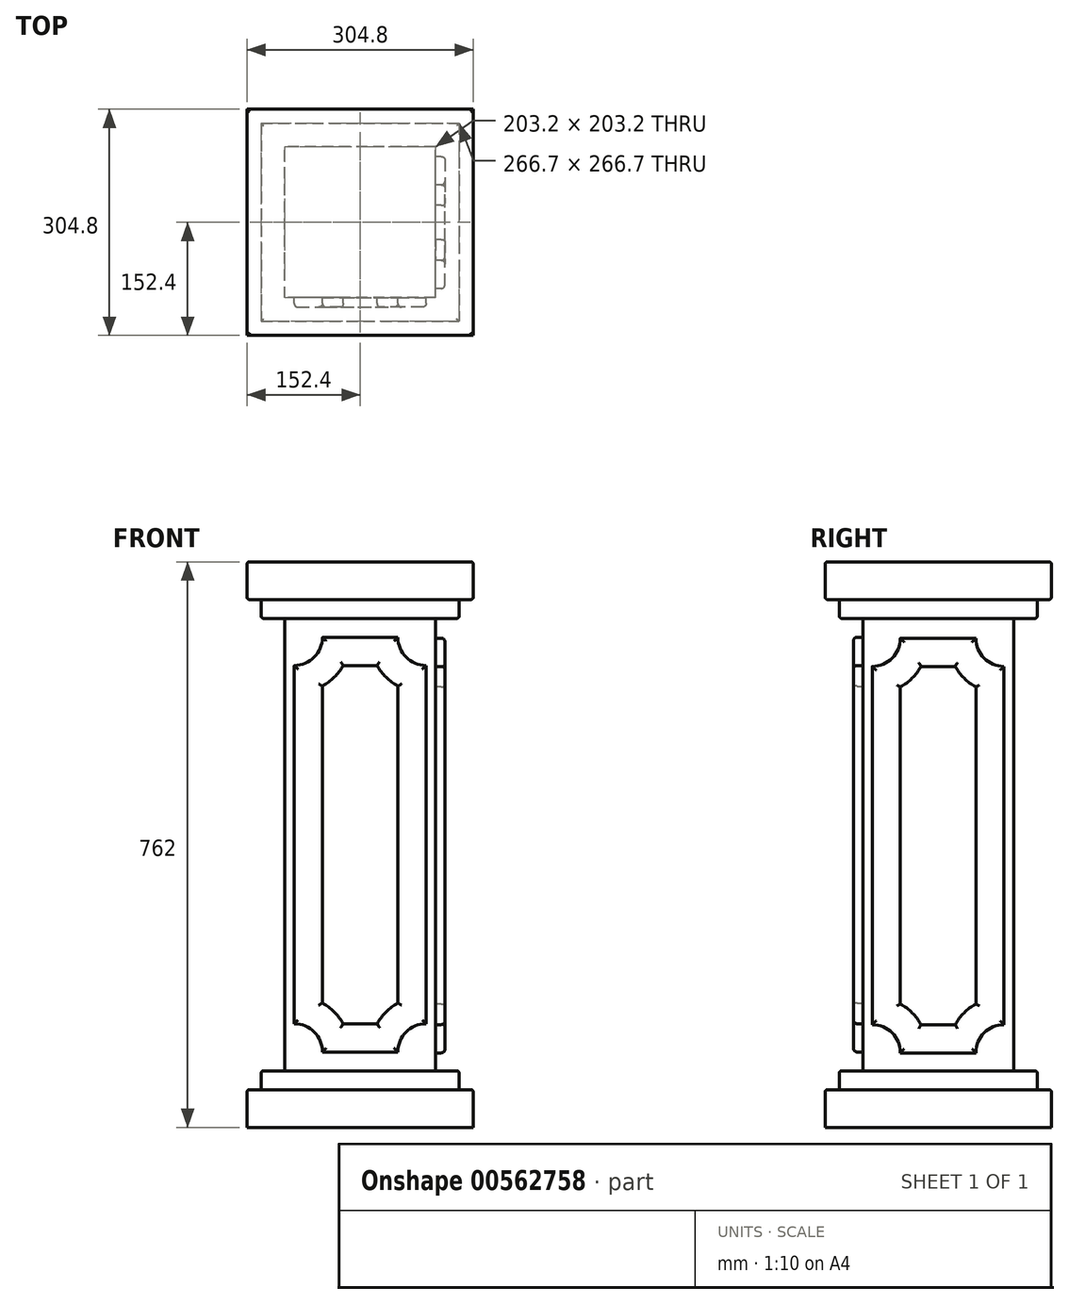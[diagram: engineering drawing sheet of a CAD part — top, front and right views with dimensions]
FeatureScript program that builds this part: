
annotation { "Feature Type Name" : "Feature", "Feature Type Description" : "" }
export const myFeature = defineFeature(function(context is Context, id is Id, definition is map)
    precondition{}
    {
        {
            var Q0;
            Q0=qCreatedBy(makeId("Top.planeOp"),FACE);
            var sketch = newSketch(context, id + "F0", { "sketchPlane" : qUnion([Q0])});
            skLineSegment(sketch, "E0.bottom", {"start": v(0, 0) * mm, "end": v(304.8, 0) * mm});
            skLineSegment(sketch, "E0.top", {"start": v(0, -304.8) * mm, "end": v(304.8, -304.8) * mm});
            skLineSegment(sketch, "E0.left", {"start": v(0, 0) * mm, "end": v(0, -304.8) * mm});
            skLineSegment(sketch, "E0.right", {"start": v(304.8, 0) * mm, "end": v(304.8, -304.8) * mm});
            skSolve(sketch);
        }
        {
            var Q0;
            Q0 = qSketchRegion(id + "F0", true);
            extrude(context, id + "F1", {"entities" : qUnion([Q0]), "depth" : 50.8 * mm, "offsetDistance" : 25.4 * mm});
        }
        {
            var Q0;
            Q0=makeQuery(id+"F1.opExtrude","CAP_FACE",FACE,{"disambiguationData":[OSD([sQuery(id+"F0.wireOp",EDGE,"E0.bottom"),sQuery(id+"F0.wireOp",EDGE,"E0.top"),sQuery(id+"F0.wireOp",EDGE,"E0.left"),sQuery(id+"F0.wireOp",EDGE,"E0.right")])],"isStart":false});
            var sketch = newSketch(context, id + "F2", { "sketchPlane" : qUnion([Q0])});
            skLineSegment(sketch, "E1.bottom", {"start": v(50.8, -50.8) * mm, "end": v(254, -50.8) * mm});
            skLineSegment(sketch, "E1.top", {"start": v(50.8, -254) * mm, "end": v(254, -254) * mm});
            skLineSegment(sketch, "E1.left", {"start": v(50.8, -50.8) * mm, "end": v(50.8, -254) * mm});
            skLineSegment(sketch, "E1.right", {"start": v(254, -50.8) * mm, "end": v(254, -254) * mm});
            skSolve(sketch);
        }
        {
            var Q0;
            Q0=makeQuery(id+"F2.imprint","IMPRINT",FACE,{"disambiguationData":[TD([[makeQuery(id+"F2.imprint","IMPRINT",EDGE,{"derivedFrom":sQuery(id+"F2.wireOp",EDGE,"E1.bottom")}),-1.0]])]});
            extrude(context, id + "F3", {"entities" : qUnion([Q0]), "operationType" : NewBodyOperationType.ADD, "depth" : 660.4 * mm, "offsetDistance" : 25.4 * mm});
        }
        {
            var Q0;
            Q0=makeQuery(id+"F3.opExtrude","CAP_FACE",FACE,{"disambiguationData":[OSD([sQuery(id+"F2.wireOp",EDGE,"E1.bottom"),sQuery(id+"F2.wireOp",EDGE,"E1.top"),sQuery(id+"F2.wireOp",EDGE,"E1.left"),sQuery(id+"F2.wireOp",EDGE,"E1.right")])],"isStart":false});
            var sketch = newSketch(context, id + "F4", { "sketchPlane" : qUnion([Q0])});
            skLineSegment(sketch, "E2.bottom", {"start": v(0, 0) * mm, "end": v(304.8, 0) * mm});
            skLineSegment(sketch, "E2.top", {"start": v(0, -304.8) * mm, "end": v(304.8, -304.8) * mm});
            skLineSegment(sketch, "E2.left", {"start": v(0, 0) * mm, "end": v(0, -304.8) * mm});
            skLineSegment(sketch, "E2.right", {"start": v(304.8, 0) * mm, "end": v(304.8, -304.8) * mm});
            skSolve(sketch);
        }
        {
            var Q0;
            Q0 = qSketchRegion(id + "F4", true);
            extrude(context, id + "F5", {"entities" : qUnion([Q0]), "operationType" : NewBodyOperationType.ADD, "depth" : 50.8 * mm, "offsetDistance" : 25.4 * mm});
        }
        {
            var Q0;
            Q0=makeQuery(id+"F1.opExtrude","CAP_FACE",FACE,{"disambiguationData":[OSD([sQuery(id+"F0.wireOp",EDGE,"E0.bottom"),sQuery(id+"F0.wireOp",EDGE,"E0.top"),sQuery(id+"F0.wireOp",EDGE,"E0.left"),sQuery(id+"F0.wireOp",EDGE,"E0.right")])],"isStart":false});
            var sketch = newSketch(context, id + "F6", { "sketchPlane" : qUnion([Q0])});
            skLineSegment(sketch, "E3.bottom", {"start": v(19.05, -19.05) * mm, "end": v(285.75, -19.05) * mm});
            skLineSegment(sketch, "E3.top", {"start": v(19.05, -285.75) * mm, "end": v(285.75, -285.75) * mm});
            skLineSegment(sketch, "E3.left", {"start": v(19.05, -19.05) * mm, "end": v(19.05, -285.75) * mm});
            skLineSegment(sketch, "E3.right", {"start": v(285.75, -19.05) * mm, "end": v(285.75, -285.75) * mm});
            skSolve(sketch);
        }
        {
            var Q0;
            Q0 = qSketchRegion(id + "F6", true);
            extrude(context, id + "F7", {"entities" : qUnion([Q0]), "operationType" : NewBodyOperationType.ADD, "depth" : 25.4 * mm, "offsetDistance" : 25.4 * mm});
        }
        {
            var Q0;
            Q0=makeQuery(id+"F5.opExtrude","CAP_FACE",FACE,{"disambiguationData":[OSD([sQuery(id+"F4.wireOp",EDGE,"E2.bottom"),sQuery(id+"F4.wireOp",EDGE,"E2.top"),sQuery(id+"F4.wireOp",EDGE,"E2.left"),sQuery(id+"F4.wireOp",EDGE,"E2.right")])],"isStart":true});
            var sketch = newSketch(context, id + "F8", { "sketchPlane" : qUnion([Q0])});
            skLineSegment(sketch, "E4.bottom", {"start": v(19.05, 285.75) * mm, "end": v(285.75, 285.75) * mm});
            skLineSegment(sketch, "E4.top", {"start": v(19.05, 19.05) * mm, "end": v(285.75, 19.05) * mm});
            skLineSegment(sketch, "E4.left", {"start": v(19.05, 285.75) * mm, "end": v(19.05, 19.05) * mm});
            skLineSegment(sketch, "E4.right", {"start": v(285.75, 285.75) * mm, "end": v(285.75, 19.05) * mm});
            skSolve(sketch);
        }
        {
            var Q0;
            Q0 = qSketchRegion(id + "F8", true);
            extrude(context, id + "F9", {"entities" : qUnion([Q0]), "operationType" : NewBodyOperationType.ADD, "depth" : 25.4 * mm, "offsetDistance" : 25.4 * mm});
        }
        {
            var Q0;
            Q0=makeQuery(id+"F7.opExtrude","CAP_EDGE",EDGE,{"disambiguationData":[OSD([sQuery(id+"F6.wireOp",EDGE,"E3.top")])],"isStart":false});
            var Q1;
            Q1=makeQuery(id+"F7.opExtrude","CAP_EDGE",EDGE,{"disambiguationData":[OSD([sQuery(id+"F6.wireOp",EDGE,"E3.right")])],"isStart":false});
            var Q2;
            Q2=makeQuery(id+"F7.opExtrude","CAP_EDGE",EDGE,{"disambiguationData":[OSD([sQuery(id+"F6.wireOp",EDGE,"E3.bottom")])],"isStart":false});
            var Q3;
            Q3=makeQuery(id+"F7.opExtrude","CAP_EDGE",EDGE,{"disambiguationData":[OSD([sQuery(id+"F6.wireOp",EDGE,"E3.left")])],"isStart":false});
            fillet(context, id + "F10", {"entities" : qUnion([Q0, Q1, Q2, Q3]), "radius" : 3.17 * mm, "tangentPropagation" : true, "allowEdgeOverflow" : false});
        }
        {
            var Q0;
            Q0=makeQuery(id+"F1.opExtrude","CAP_EDGE",EDGE,{"disambiguationData":[OSD([sQuery(id+"F0.wireOp",EDGE,"E0.right")])],"isStart":false});
            var Q1;
            Q1=makeQuery(id+"F1.opExtrude","CAP_EDGE",EDGE,{"disambiguationData":[OSD([sQuery(id+"F0.wireOp",EDGE,"E0.top")])],"isStart":false});
            var Q2;
            Q2=makeQuery(id+"F1.opExtrude","CAP_EDGE",EDGE,{"disambiguationData":[OSD([sQuery(id+"F0.wireOp",EDGE,"E0.left")])],"isStart":false});
            var Q3;
            Q3=makeQuery(id+"F1.opExtrude","CAP_EDGE",EDGE,{"disambiguationData":[OSD([sQuery(id+"F0.wireOp",EDGE,"E0.bottom")])],"isStart":false});
            fillet(context, id + "F11", {"entities" : qUnion([Q0, Q1, Q2, Q3]), "radius" : 3.17 * mm, "tangentPropagation" : true, "allowEdgeOverflow" : false});
        }
        {
            var Q0;
            Q0=makeQuery(id+"F9.opExtrude","CAP_EDGE",EDGE,{"disambiguationData":[OSD([sQuery(id+"F8.wireOp",EDGE,"E4.right")])],"isStart":false});
            var Q1;
            Q1=makeQuery(id+"F9.opExtrude","CAP_EDGE",EDGE,{"disambiguationData":[OSD([sQuery(id+"F8.wireOp",EDGE,"E4.bottom")])],"isStart":false});
            var Q2;
            Q2=makeQuery(id+"F9.opExtrude","CAP_EDGE",EDGE,{"disambiguationData":[OSD([sQuery(id+"F8.wireOp",EDGE,"E4.left")])],"isStart":false});
            var Q3;
            Q3=makeQuery(id+"F9.opExtrude","CAP_EDGE",EDGE,{"disambiguationData":[OSD([sQuery(id+"F8.wireOp",EDGE,"E4.top")])],"isStart":false});
            fillet(context, id + "F12", {"entities" : qUnion([Q0, Q1, Q2, Q3]), "radius" : 3.17 * mm, "tangentPropagation" : true, "allowEdgeOverflow" : false});
        }
        {
            var Q0;
            Q0=makeQuery(id+"F5.opExtrude","CAP_EDGE",EDGE,{"disambiguationData":[OSD([sQuery(id+"F4.wireOp",EDGE,"E2.top")])],"isStart":true});
            var Q1;
            Q1=makeQuery(id+"F5.opExtrude","CAP_EDGE",EDGE,{"disambiguationData":[OSD([sQuery(id+"F4.wireOp",EDGE,"E2.left")])],"isStart":true});
            var Q2;
            Q2=makeQuery(id+"F5.opExtrude","CAP_EDGE",EDGE,{"disambiguationData":[OSD([sQuery(id+"F4.wireOp",EDGE,"E2.bottom")])],"isStart":true});
            var Q3;
            Q3=makeQuery(id+"F5.opExtrude","CAP_EDGE",EDGE,{"disambiguationData":[OSD([sQuery(id+"F4.wireOp",EDGE,"E2.right")])],"isStart":true});
            fillet(context, id + "F13", {"entities" : qUnion([Q0, Q1, Q2, Q3]), "radius" : 3.17 * mm, "tangentPropagation" : true, "allowEdgeOverflow" : false});
        }
        {
            var Q0;
            Q0=makeQuery(id+"F3.opExtrude","SWEPT_FACE",FACE,{"disambiguationData":[OSD([sQuery(id+"F2.wireOp",EDGE,"E1.top")])]});
            var sketch = newSketch(context, id + "F14", { "sketchPlane" : qUnion([Q0])});
            skArc(sketch, "E5", {"start": v(63.5, 622.3) * mm, "mid": v(90.44, 633.46) * mm, "end": v(101.6, 660.4) * mm});
            skArc(sketch, "E6", {"start": v(203.2, 660.4) * mm, "mid": v(214.36, 633.46) * mm, "end": v(241.3, 622.3) * mm});
            skLineSegment(sketch, "E7", {"start": v(101.6, 660.4) * mm, "end": v(203.2, 660.4) * mm});
            skArc(sketch, "E8", {"start": v(63.5, 139.7) * mm, "mid": v(90.44, 128.54) * mm, "end": v(101.6, 101.6) * mm});
            skArc(sketch, "E9", {"start": v(203.2, 101.6) * mm, "mid": v(214.36, 128.54) * mm, "end": v(241.3, 139.7) * mm});
            skLineSegment(sketch, "E10", {"start": v(101.6, 101.6) * mm, "end": v(203.2, 101.6) * mm});
            skLineSegment(sketch, "E11", {"start": v(63.5, 139.7) * mm, "end": v(63.5, 622.3) * mm});
            skLineSegment(sketch, "E12", {"start": v(241.3, 622.3) * mm, "end": v(241.3, 139.7) * mm});
            skLineSegment(sketch, "E13", {"start": v(50.8, 373.92) * mm, "end": v(50.8, 596.34) * mm, "construction": true});
            skLineSegment(sketch, "E14", {"start": v(254, 370.37) * mm, "end": v(254, 598.7) * mm, "construction": true});
            skLineSegment(sketch, "E15", {"start": v(50.8, 76.2) * mm, "end": v(254, 76.2) * mm, "construction": true});
            skLineSegment(sketch, "E16", {"start": v(50.8, 685.8) * mm, "end": v(254, 685.8) * mm, "construction": true});
            skLineSegment(sketch, "E17.0", {"start": v(101.6, 167.6) * mm, "end": v(101.6, 594.4) * mm});
            skArc(sketch, "E17.1", {"start": v(101.6, 167.6) * mm, "mid": v(117.38, 155.48) * mm, "end": v(129.5, 139.7) * mm});
            skArc(sketch, "E17.2", {"start": v(101.6, 594.4) * mm, "mid": v(117.38, 606.52) * mm, "end": v(129.5, 622.3) * mm});
            skLineSegment(sketch, "E17.3", {"start": v(129.5, 139.7) * mm, "end": v(175.3, 139.7) * mm});
            skLineSegment(sketch, "E17.4", {"start": v(129.5, 622.3) * mm, "end": v(175.3, 622.3) * mm});
            skArc(sketch, "E17.5", {"start": v(175.3, 622.3) * mm, "mid": v(187.42, 606.52) * mm, "end": v(203.2, 594.4) * mm});
            skLineSegment(sketch, "E17.6", {"start": v(203.2, 594.4) * mm, "end": v(203.2, 167.6) * mm});
            skArc(sketch, "E17.7", {"start": v(175.3, 139.7) * mm, "mid": v(187.42, 155.48) * mm, "end": v(203.2, 167.6) * mm});
            skSolve(sketch);
        }
        {
            var Q0;
            Q0 = qSketchRegion(id + "F14", true);
            extrude(context, id + "F15", {"entities" : qUnion([Q0]), "operationType" : NewBodyOperationType.ADD, "depth" : 12.7 * mm, "offsetDistance" : 25.4 * mm});
        }
        {
            var Q0;
            Q0=makeQuery(id+"F3.opExtrude","SWEPT_FACE",FACE,{"disambiguationData":[OSD([sQuery(id+"F2.wireOp",EDGE,"E1.right")])]});
            var sketch = newSketch(context, id + "F16", { "sketchPlane" : qUnion([Q0])});
            skLineSegment(sketch, "E18", {"start": v(-101.6, -338.04) * mm, "end": v(101.6, -338.04) * mm, "construction": true});
            skLineSegment(sketch, "E19", {"start": v(-101.6, 685.8) * mm, "end": v(101.6, 685.8) * mm, "construction": true});
            skArc(sketch, "E20", {"start": v(-241.47, 621.09) * mm, "mid": v(-214.53, 632.25) * mm, "end": v(-203.37, 659.19) * mm});
            skArc(sketch, "E21", {"start": v(-101.77, 659.19) * mm, "mid": v(-90.6, 632.25) * mm, "end": v(-63.67, 621.09) * mm});
            skLineSegment(sketch, "E22", {"start": v(-203.37, 659.19) * mm, "end": v(-101.77, 659.19) * mm});
            skArc(sketch, "E23", {"start": v(-241.47, 138.49) * mm, "mid": v(-214.53, 127.33) * mm, "end": v(-203.37, 100.39) * mm});
            skArc(sketch, "E24", {"start": v(-101.77, 100.39) * mm, "mid": v(-90.6, 127.33) * mm, "end": v(-63.67, 138.49) * mm});
            skLineSegment(sketch, "E25", {"start": v(-203.37, 100.39) * mm, "end": v(-101.77, 100.39) * mm});
            skLineSegment(sketch, "E26", {"start": v(-241.47, 138.49) * mm, "end": v(-241.47, 621.09) * mm});
            skLineSegment(sketch, "E27", {"start": v(-63.67, 621.09) * mm, "end": v(-63.67, 138.49) * mm});
            skLineSegment(sketch, "E28", {"start": v(-254.17, 372.7) * mm, "end": v(-254.17, 595.13) * mm, "construction": true});
            skLineSegment(sketch, "E29", {"start": v(-50.97, 369.16) * mm, "end": v(-50.97, 597.5) * mm, "construction": true});
            skLineSegment(sketch, "E30", {"start": v(-254.17, 74.99) * mm, "end": v(-50.97, 74.99) * mm, "construction": true});
            skLineSegment(sketch, "E31", {"start": v(-254.17, 684.59) * mm, "end": v(-50.97, 684.59) * mm, "construction": true});
            skLineSegment(sketch, "E32.0", {"start": v(-203.37, 166.38) * mm, "end": v(-203.37, 593.2) * mm});
            skArc(sketch, "E32.1", {"start": v(-203.37, 166.38) * mm, "mid": v(-187.59, 154.27) * mm, "end": v(-175.48, 138.49) * mm});
            skArc(sketch, "E32.2", {"start": v(-203.37, 593.2) * mm, "mid": v(-187.59, 605.3) * mm, "end": v(-175.48, 621.09) * mm});
            skLineSegment(sketch, "E32.3", {"start": v(-175.48, 138.49) * mm, "end": v(-129.66, 138.49) * mm});
            skLineSegment(sketch, "E32.4", {"start": v(-175.48, 621.09) * mm, "end": v(-129.66, 621.09) * mm});
            skArc(sketch, "E32.5", {"start": v(-129.66, 621.09) * mm, "mid": v(-117.55, 605.3) * mm, "end": v(-101.77, 593.2) * mm});
            skLineSegment(sketch, "E32.6", {"start": v(-101.77, 593.2) * mm, "end": v(-101.77, 166.38) * mm});
            skArc(sketch, "E32.7", {"start": v(-129.66, 138.49) * mm, "mid": v(-117.55, 154.27) * mm, "end": v(-101.77, 166.38) * mm});
            skSolve(sketch);
        }
        {
            var Q0;
            Q0 = qSketchRegion(id + "F16", true);
            extrude(context, id + "F17", {"entities" : qUnion([Q0]), "operationType" : NewBodyOperationType.ADD, "depth" : 12.7 * mm, "offsetDistance" : 25.4 * mm});
        }
        {
            var Q0;
            Q0=makeQuery(id+"F5.opExtrude","CAP_FACE",FACE,{"disambiguationData":[OSD([sQuery(id+"F4.wireOp",EDGE,"E2.bottom"),sQuery(id+"F4.wireOp",EDGE,"E2.top"),sQuery(id+"F4.wireOp",EDGE,"E2.left"),sQuery(id+"F4.wireOp",EDGE,"E2.right")])],"isStart":false});
            fillet(context, id + "F18", {"entities" : qUnion([Q0]), "radius" : 3.17 * mm, "tangentPropagation" : true, "allowEdgeOverflow" : false});
        }
        {
            var Q0;
            Q0=makeQuery(id+"F15.opExtrude","CAP_FACE",FACE,{"disambiguationData":[OSD([sQuery(id+"F14.wireOp",EDGE,"E5"),sQuery(id+"F14.wireOp",EDGE,"E6"),sQuery(id+"F14.wireOp",EDGE,"E7"),sQuery(id+"F14.wireOp",EDGE,"E8"),sQuery(id+"F14.wireOp",EDGE,"E9"),sQuery(id+"F14.wireOp",EDGE,"E10"),sQuery(id+"F14.wireOp",EDGE,"E11"),sQuery(id+"F14.wireOp",EDGE,"E12"),sQuery(id+"F14.wireOp",EDGE,"E17.0"),sQuery(id+"F14.wireOp",EDGE,"E17.1"),sQuery(id+"F14.wireOp",EDGE,"E17.2"),sQuery(id+"F14.wireOp",EDGE,"E17.3"),sQuery(id+"F14.wireOp",EDGE,"E17.4"),sQuery(id+"F14.wireOp",EDGE,"E17.5"),sQuery(id+"F14.wireOp",EDGE,"E17.6"),sQuery(id+"F14.wireOp",EDGE,"E17.7")])],"isStart":false});
            fillet(context, id + "F19", {"entities" : qUnion([Q0]), "radius" : 5.08 * mm, "tangentPropagation" : true, "allowEdgeOverflow" : false});
        }
        {
            var Q0;
            Q0=makeQuery(id+"F17.opExtrude","CAP_FACE",FACE,{"disambiguationData":[OSD([sQuery(id+"F16.wireOp",EDGE,"E20"),sQuery(id+"F16.wireOp",EDGE,"E21"),sQuery(id+"F16.wireOp",EDGE,"E22"),sQuery(id+"F16.wireOp",EDGE,"E23"),sQuery(id+"F16.wireOp",EDGE,"E24"),sQuery(id+"F16.wireOp",EDGE,"E25"),sQuery(id+"F16.wireOp",EDGE,"E26"),sQuery(id+"F16.wireOp",EDGE,"E27"),sQuery(id+"F16.wireOp",EDGE,"E32.0"),sQuery(id+"F16.wireOp",EDGE,"E32.1"),sQuery(id+"F16.wireOp",EDGE,"E32.2"),sQuery(id+"F16.wireOp",EDGE,"E32.3"),sQuery(id+"F16.wireOp",EDGE,"E32.4"),sQuery(id+"F16.wireOp",EDGE,"E32.5"),sQuery(id+"F16.wireOp",EDGE,"E32.6"),sQuery(id+"F16.wireOp",EDGE,"E32.7")])],"isStart":false});
            fillet(context, id + "F20", {"entities" : qUnion([Q0]), "radius" : 5.08 * mm, "tangentPropagation" : true, "allowEdgeOverflow" : false});
        }
    });
